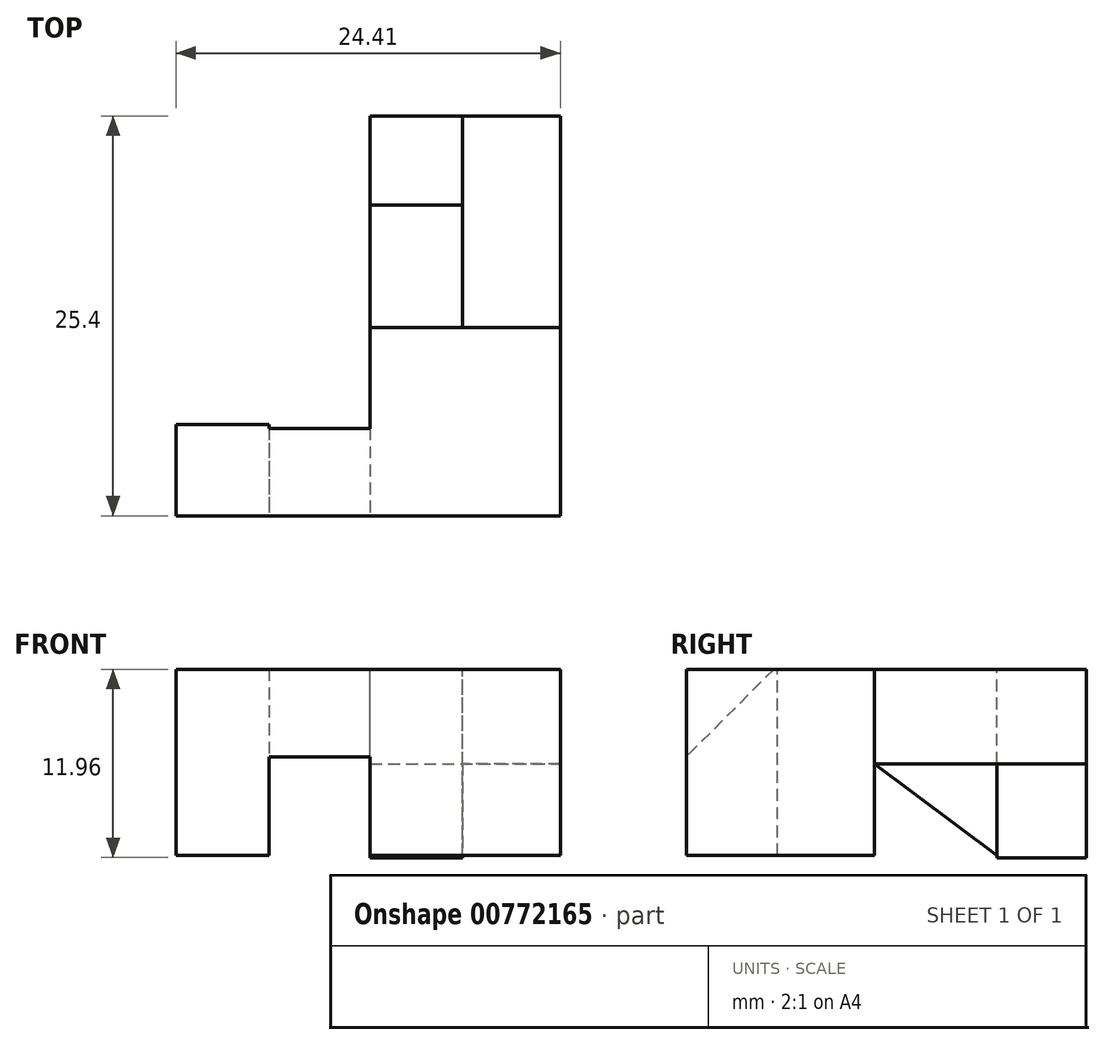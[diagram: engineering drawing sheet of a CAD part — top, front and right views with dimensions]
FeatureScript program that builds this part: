
annotation { "Feature Type Name" : "Feature", "Feature Type Description" : "" }
export const myFeature = defineFeature(function(context is Context, id is Id, definition is map)
    precondition{}
    {
        {
            var Q0;
            Q0=qCreatedBy(makeId("Top.planeOp"),FACE);
            var sketch = newSketch(context, id + "F0", { "sketchPlane" : qUnion([Q0])});
            skLineSegment(sketch, "E0.bottom", {"start": v(0, 0) * mm, "end": v(12.1, 0) * mm});
            skLineSegment(sketch, "E0.top", {"start": v(0, -11.96) * mm, "end": v(12.1, -11.96) * mm});
            skLineSegment(sketch, "E0.left", {"start": v(0, 0) * mm, "end": v(0, -11.96) * mm});
            skLineSegment(sketch, "E1", {"start": v(5.87, 13.44) * mm, "end": v(5.87, 7.77) * mm});
            skLineSegment(sketch, "E2", {"start": v(5.87, 7.77) * mm, "end": v(0, 7.77) * mm});
            skLineSegment(sketch, "E3", {"start": v(5.87, 7.77) * mm, "end": v(5.87, 0) * mm});
            skLineSegment(sketch, "E4", {"start": v(0, 13.44) * mm, "end": v(0, 0) * mm});
            skLineSegment(sketch, "E5", {"start": v(0, -11.96) * mm, "end": v(-12.32, -11.96) * mm});
            skLineSegment(sketch, "E6", {"start": v(-12.32, -11.96) * mm, "end": v(-12.32, -6.17) * mm});
            skLineSegment(sketch, "E7", {"start": v(-12.32, -6.17) * mm, "end": v(-6.4, -6.17) * mm});
            skLineSegment(sketch, "E8", {"start": v(-6.4, -6.17) * mm, "end": v(0, -6.17) * mm});
            skLineSegment(sketch, "E9", {"start": v(-6.4, -6.17) * mm, "end": v(-6.4, -11.96) * mm});
            skLineSegment(sketch, "E10", {"start": v(12.1, -11.96) * mm, "end": v(12.1, 13.44) * mm});
            skLineSegment(sketch, "E11", {"start": v(12.1, 13.44) * mm, "end": v(0, 13.44) * mm});
            skSolve(sketch);
        }
        {
            var Q0;
            {var subQ0=sQuery(id+"F0.wireOp",EDGE,"bSB4M555-EzEe-Ix5s-z5l3-pP4607UdG9xA");Q0=makeQuery(id+"F0.imprint","IMPRINT",FACE,{"disambiguationData":[TD([[makeQuery(id+"F0.imprint","IMPRINT",EDGE,{"derivedFrom":subQ0}),-1.0]])]});}
            var Q1;
            {var subQ4=sQuery(id+"F0.wireOp",EDGE,"E0.top");Q1=makeQuery(id+"F0.imprint","IMPRINT",FACE,{"disambiguationData":[TD([[makeQuery(id+"F0.imprint","IMPRINT",EDGE,{"derivedFrom":subQ4}),1.0]])]});}
            var Q2;
            {var subQ0=sQuery(id+"F0.wireOp",EDGE,"E6");Q2=makeQuery(id+"F0.imprint","IMPRINT",FACE,{"disambiguationData":[TD([[makeQuery(id+"F0.imprint","IMPRINT",EDGE,{"derivedFrom":subQ0}),-1.0]])]});}
            extrude(context, id + "F1", {"entities" : qUnion([Q0, Q1, Q2]), "oppositeDirection" : true, "depth" : 11.8 * mm, "offsetDistance" : 25.4 * mm});
        }
        {
            var Q0;
            {var subQ6=sQuery(id+"F0.wireOp",EDGE,"E1");Q0=makeQuery(id+"F0.imprint","IMPRINT",FACE,{"disambiguationData":[TD([[makeQuery(id+"F0.imprint","IMPRINT",EDGE,{"derivedFrom":subQ6}),1.0]])]});}
            var Q1;
            {var subQ4=sQuery(id+"F0.wireOp",EDGE,"E2");Q1=makeQuery(id+"F0.imprint","IMPRINT",FACE,{"disambiguationData":[TD([[makeQuery(id+"F0.imprint","IMPRINT",EDGE,{"derivedFrom":subQ4}),1.0]])]});}
            extrude(context, id + "F2", {"entities" : qUnion([Q0, Q1]), "oppositeDirection" : true, "depth" : 6 * mm, "offsetDistance" : 25.4 * mm});
        }
        {
            var Q0;
            Q0=makeQuery(id+"F1.opExtrude","SWEPT_FACE",FACE,{"disambiguationData":[OSD([sQuery(id+"F0.wireOp",EDGE,"E0.left")])]});
            var sketch = newSketch(context, id + "F3", { "sketchPlane" : qUnion([Q0])});
            skLineSegment(sketch, "E12", {"start": v(11.96, 0) * mm, "end": v(11.96, -5.56) * mm});
            skLineSegment(sketch, "E13", {"start": v(11.96, 0) * mm, "end": v(6.4, 0) * mm});
            skLineSegment(sketch, "E14", {"start": v(6.4, 0) * mm, "end": v(11.96, -5.56) * mm});
            skSolve(sketch);
        }
        {
            var Q0;
            {var subQ4=sQuery(id+"F0.wireOp",EDGE,"E2");Q0=makeQuery(id+"F0.imprint","IMPRINT",FACE,{"disambiguationData":[TD([[makeQuery(id+"F0.imprint","IMPRINT",EDGE,{"derivedFrom":subQ4}),1.0]])]});}
            var Q1;
            Q1=makeQuery(id+"F2.opExtrude","CAP_FACE",FACE,{"disambiguationData":[OSD([sQuery(id+"F0.wireOp",EDGE,"E0.bottom"),sQuery(id+"F0.wireOp",EDGE,"TZ8VIxX6-mhEG-DA63-i186-NkoxIQWt5nIF"),sQuery(id+"F0.wireOp",EDGE,"FWkBh8Dm-K7Wm-a6I6-4Plz-l2MyKIOzHpR4"),sQuery(id+"F0.wireOp",EDGE,"E1"),sQuery(id+"F0.wireOp",EDGE,"E3")])],"isStart":false});
            extrude(context, id + "F4", {"entities" : qUnion([Q0]), "endBound" : BoundingType.UP_TO_SURFACE, "oppositeDirection" : true, "depth" : 25.4 * mm, "endBoundEntityFace" : qUnion([Q1]), "offsetDistance" : 25.4 * mm});
        }
        {
            var Q0;
            Q0=makeQuery(id+"F4.opExtrude","SWEPT_FACE",FACE,{"disambiguationData":[OSD([sQuery(id+"F0.wireOp",EDGE,"E4")])]});
            var sketch = newSketch(context, id + "F5", { "sketchPlane" : qUnion([Q0])});
            skLineSegment(sketch, "E15", {"start": v(0, -6) * mm, "end": v(-7.77, -6) * mm});
            skLineSegment(sketch, "E16", {"start": v(-7.77, -6) * mm, "end": v(-7.77, -11.81) * mm});
            skLineSegment(sketch, "E17", {"start": v(-7.77, -11.81) * mm, "end": v(0, -6) * mm});
            skSolve(sketch);
        }
        {
            var Q0;
            Q0=makeQuery(id+"F5.imprint","IMPRINT",FACE,{"disambiguationData":[TD([[makeQuery(id+"F5.imprint","IMPRINT",EDGE,{"derivedFrom":sQuery(id+"F5.wireOp",EDGE,"E15")}),1.0]])]});
            var Q1;
            Q1=makeQuery(id+"F2.opExtrude","SWEPT_FACE",FACE,{"disambiguationData":[OSD([sQuery(id+"F0.wireOp",EDGE,"E1")])]});
            extrude(context, id + "F6", {"entities" : qUnion([Q0]), "endBound" : BoundingType.UP_TO_SURFACE, "oppositeDirection" : true, "depth" : 25.4 * mm, "endBoundEntityFace" : qUnion([Q1]), "offsetDistance" : 25.4 * mm});
        }
        {
            var Q0;
            {var subQ0=sQuery(id+"F0.wireOp",EDGE,"E1");Q0=makeQuery(id+"F0.imprint","IMPRINT",FACE,{"disambiguationData":[TD([[makeQuery(id+"F0.imprint","IMPRINT",EDGE,{"derivedFrom":subQ0}),-1.0]])]});}
            extrude(context, id + "F7", {"entities" : qUnion([Q0]), "oppositeDirection" : true, "depth" : 11.96 * mm, "offsetDistance" : 25.4 * mm});
        }
        {
            var Q0;
            Q0=makeQuery(id+"F3.imprint","IMPRINT",FACE,{"disambiguationData":[TD([[makeQuery(id+"F3.imprint","IMPRINT",EDGE,{"derivedFrom":sQuery(id+"F3.wireOp",EDGE,"E12")}),1.0]])]});
            var Q1;
            Q1=makeQuery(id+"F1.opExtrude","SWEPT_FACE",FACE,{"disambiguationData":[OSD([sQuery(id+"F0.wireOp",EDGE,"E9")])]});
            extrude(context, id + "F8", {"entities" : qUnion([Q0]), "operationType" : NewBodyOperationType.ADD, "endBound" : BoundingType.UP_TO_SURFACE, "depth" : 25.4 * mm, "endBoundEntityFace" : qUnion([Q1]), "offsetDistance" : 25.4 * mm});
        }
    });
